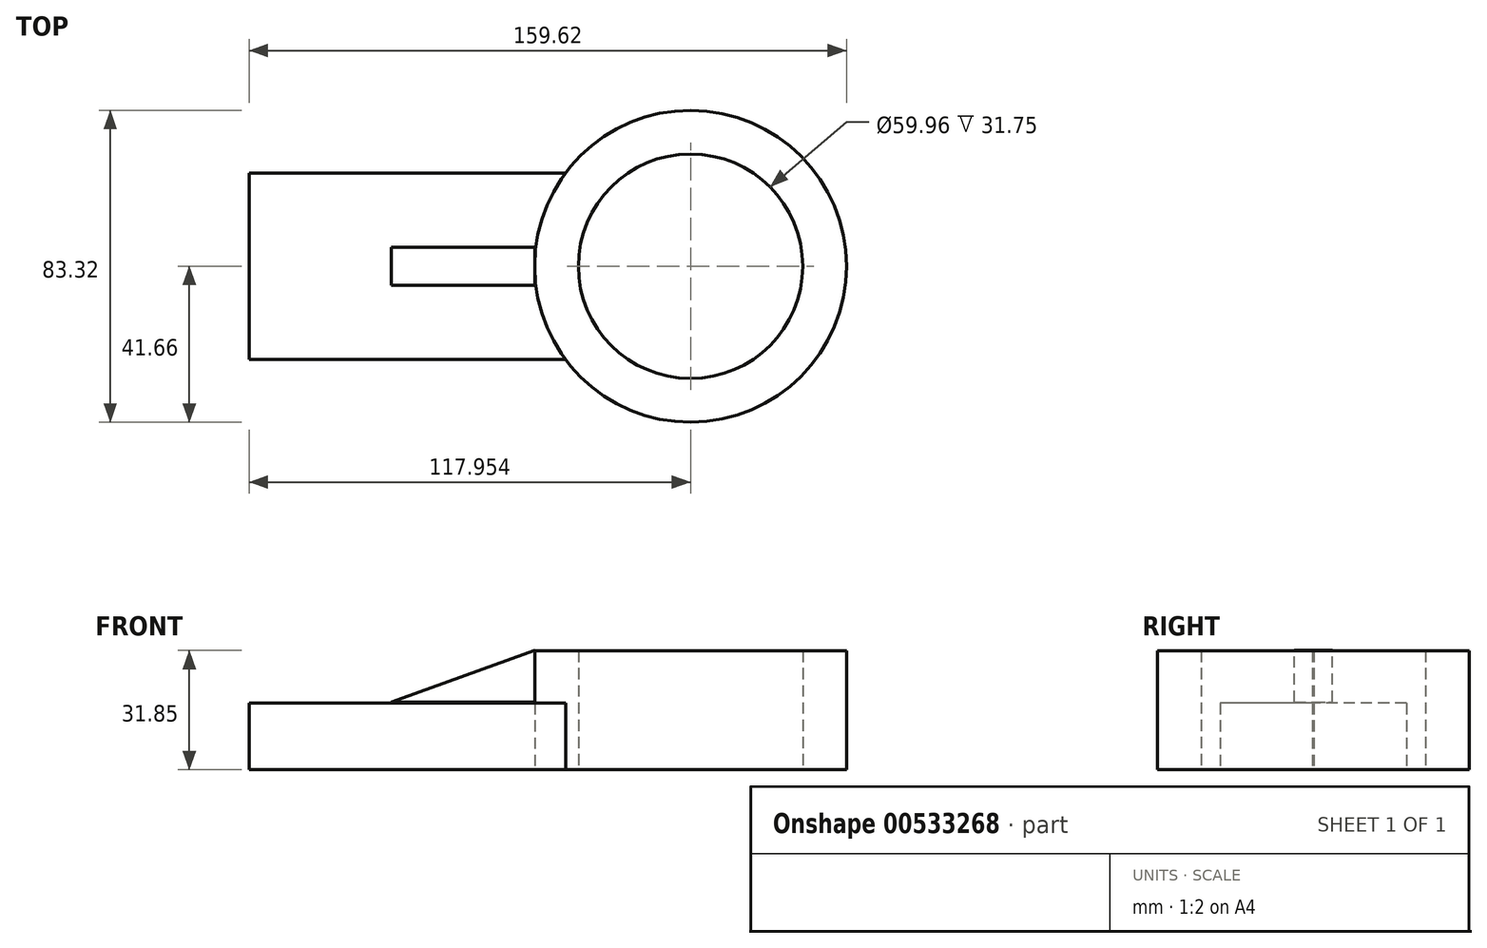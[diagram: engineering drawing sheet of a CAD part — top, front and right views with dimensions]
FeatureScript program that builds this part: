
annotation { "Feature Type Name" : "Feature", "Feature Type Description" : "" }
export const myFeature = defineFeature(function(context is Context, id is Id, definition is map)
    precondition{}
    {
        {
            var Q0;
            Q0=qCreatedBy(makeId("Top.planeOp"),FACE);
            var sketch = newSketch(context, id + "F0", { "sketchPlane" : qUnion([Q0])});
            skCircle(sketch, "E0", {"center": v(41.66, 0) * mm, "radius": 41.66 * mm});
            skCircle(sketch, "E1.0", {"center": v(41.66, 0) * mm, "radius": 29.98 * mm});
            skLineSegment(sketch, "E2.bottom", {"start": v(-76.3, 24.89) * mm, "end": v(0, 24.89) * mm});
            skLineSegment(sketch, "E2.top", {"start": v(-76.3, 0) * mm, "end": v(0, 0) * mm});
            skLineSegment(sketch, "E2.left", {"start": v(-76.3, 24.89) * mm, "end": v(-76.3, 0) * mm});
            skLineSegment(sketch, "E2.right", {"start": v(0, 24.89) * mm, "end": v(0, 0) * mm});
            skLineSegment(sketch, "E3.top", {"start": v(-76.3, -24.89) * mm, "end": v(0, -24.89) * mm});
            skLineSegment(sketch, "E3.left", {"start": v(-76.3, 0) * mm, "end": v(-76.3, -24.89) * mm});
            skLineSegment(sketch, "E3.right", {"start": v(0, 0) * mm, "end": v(0, -24.89) * mm});
            skLineSegment(sketch, "E4", {"start": v(0, -24.89) * mm, "end": v(8.25, -24.89) * mm});
            skLineSegment(sketch, "E5", {"start": v(0, 24.89) * mm, "end": v(8.25, 24.89) * mm});
            skSolve(sketch);
        }
        {
            var Q0;
            Q0=makeQuery(id+"F0.imprint","IMPRINT",FACE,{"disambiguationData":[TD([[makeQuery(id+"F0.imprint","IMPRINT",EDGE,{"derivedFrom":sQuery(id+"F0.wireOp",EDGE,"E1.0")}),-1.0]])]});
            extrude(context, id + "F1", {"entities" : qUnion([Q0]), "depth" : 31.75 * mm, "offsetDistance" : 25.4 * mm});
        }
        {
            var Q0;
            Q0 = qSketchRegion(id + "F0", true);
            extrude(context, id + "F2", {"entities" : qUnion([Q0]), "operationType" : NewBodyOperationType.ADD, "depth" : 17.78 * mm, "offsetDistance" : 25.4 * mm});
        }
        {
            var Q0;
            Q0=qCreatedBy(makeId("Front.planeOp"),FACE);
            var sketch = newSketch(context, id + "F3", { "sketchPlane" : qUnion([Q0])});
            skLineSegment(sketch, "E6", {"start": v(-38.3, 18.1) * mm, "end": v(0, 31.85) * mm});
            skLineSegment(sketch, "E7", {"start": v(-38.3, 18.1) * mm, "end": v(0, 18.1) * mm});
            skLineSegment(sketch, "E8", {"start": v(0, 18.1) * mm, "end": v(0, 31.85) * mm});
            skSolve(sketch);
        }
        {
            var Q0;
            Q0=makeQuery(id+"F3.imprint","IMPRINT",FACE,{"disambiguationData":[TD([[makeQuery(id+"F3.imprint","IMPRINT",EDGE,{"derivedFrom":sQuery(id+"F3.wireOp",EDGE,"E6")}),-1.0]])]});
            extrude(context, id + "F4", {"entities" : qUnion([Q0]), "operationType" : NewBodyOperationType.ADD, "endBound" : BoundingType.SYMMETRIC, "depth" : 10.16 * mm, "offsetDistance" : 25.4 * mm});
        }
    });
